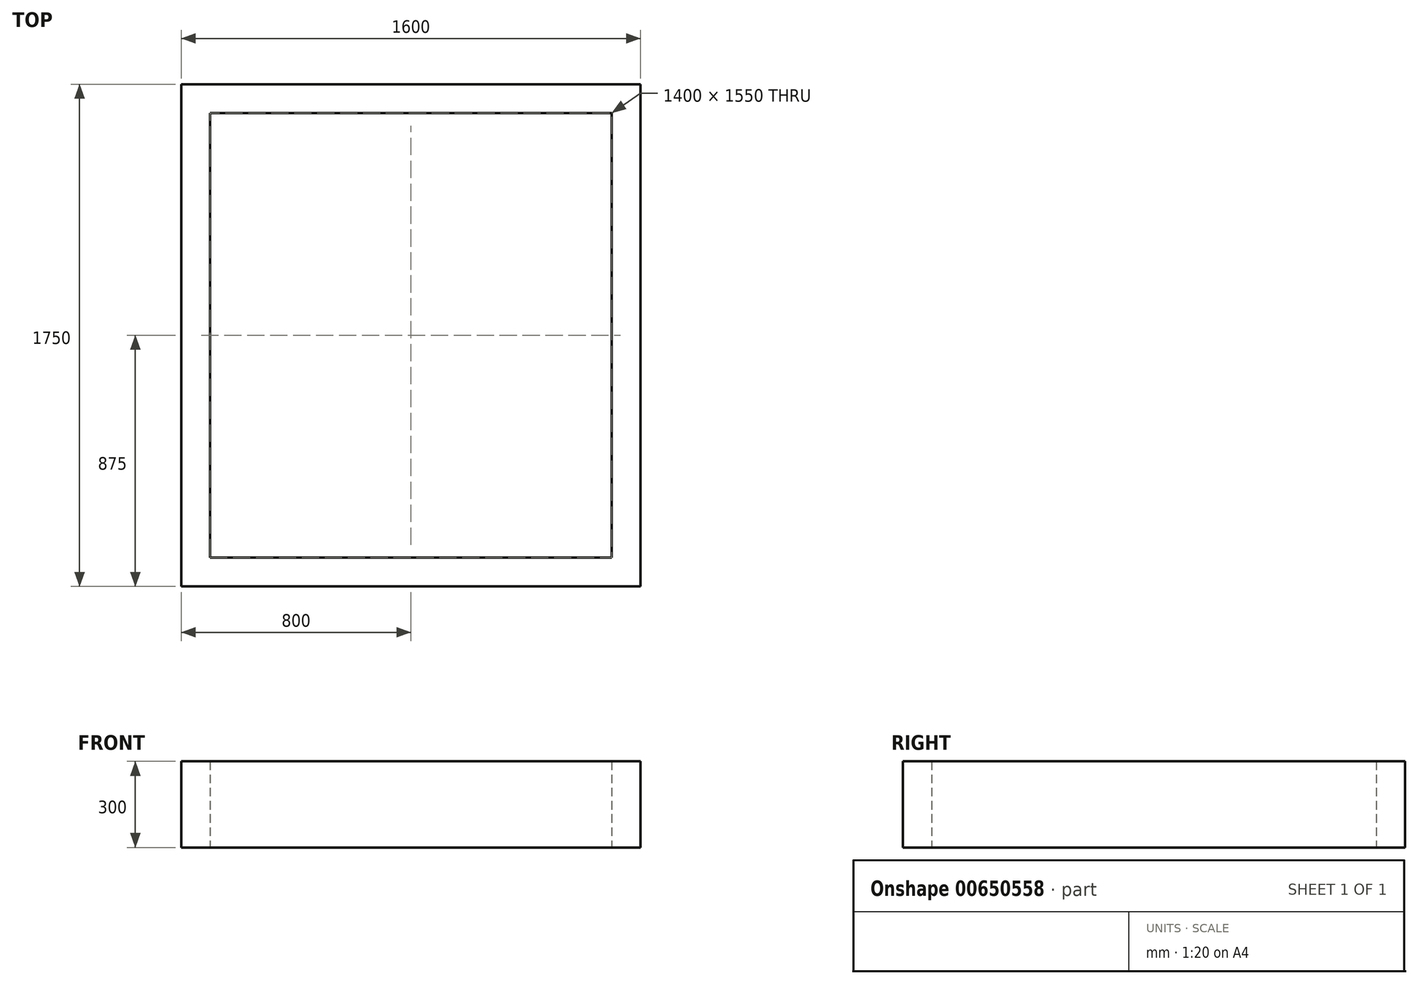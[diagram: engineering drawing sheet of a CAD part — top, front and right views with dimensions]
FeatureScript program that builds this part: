
annotation { "Feature Type Name" : "Feature", "Feature Type Description" : "" }
export const myFeature = defineFeature(function(context is Context, id is Id, definition is map)
    precondition{}
    {
        {
            var Q0;
            Q0=qCreatedBy(makeId("Top.planeOp"),FACE);
            var sketch = newSketch(context, id + "F0", { "sketchPlane" : qUnion([Q0]), "disableImprinting" : false});
            skLineSegment(sketch, "E0.bottom", {"start": v(0, 0) * mm, "end": v(-1600, 0) * mm});
            skLineSegment(sketch, "E0.top", {"start": v(0, 1750) * mm, "end": v(-1600, 1750) * mm});
            skLineSegment(sketch, "E0.left", {"start": v(0, 0) * mm, "end": v(0, 1750) * mm});
            skLineSegment(sketch, "E0.right", {"start": v(-1600, 0) * mm, "end": v(-1600, 1750) * mm});
            skLineSegment(sketch, "E1.bottom", {"start": v(-100, 100) * mm, "end": v(-1500, 100) * mm});
            skLineSegment(sketch, "E1.top", {"start": v(-100, 1650) * mm, "end": v(-1500, 1650) * mm});
            skLineSegment(sketch, "E1.left", {"start": v(-100, 100) * mm, "end": v(-100, 1650) * mm});
            skLineSegment(sketch, "E1.right", {"start": v(-1500, 100) * mm, "end": v(-1500, 1650) * mm});
            skSolve(sketch);
        }
        {
            var Q0;
            Q0=qSketchRegion(id+"F0",true);
            extrude(context, id + "F1", {"entities" : qUnion([Q0]), "depth" : 300 * mm, "offsetDistance" : 25 * mm});
        }
    });
